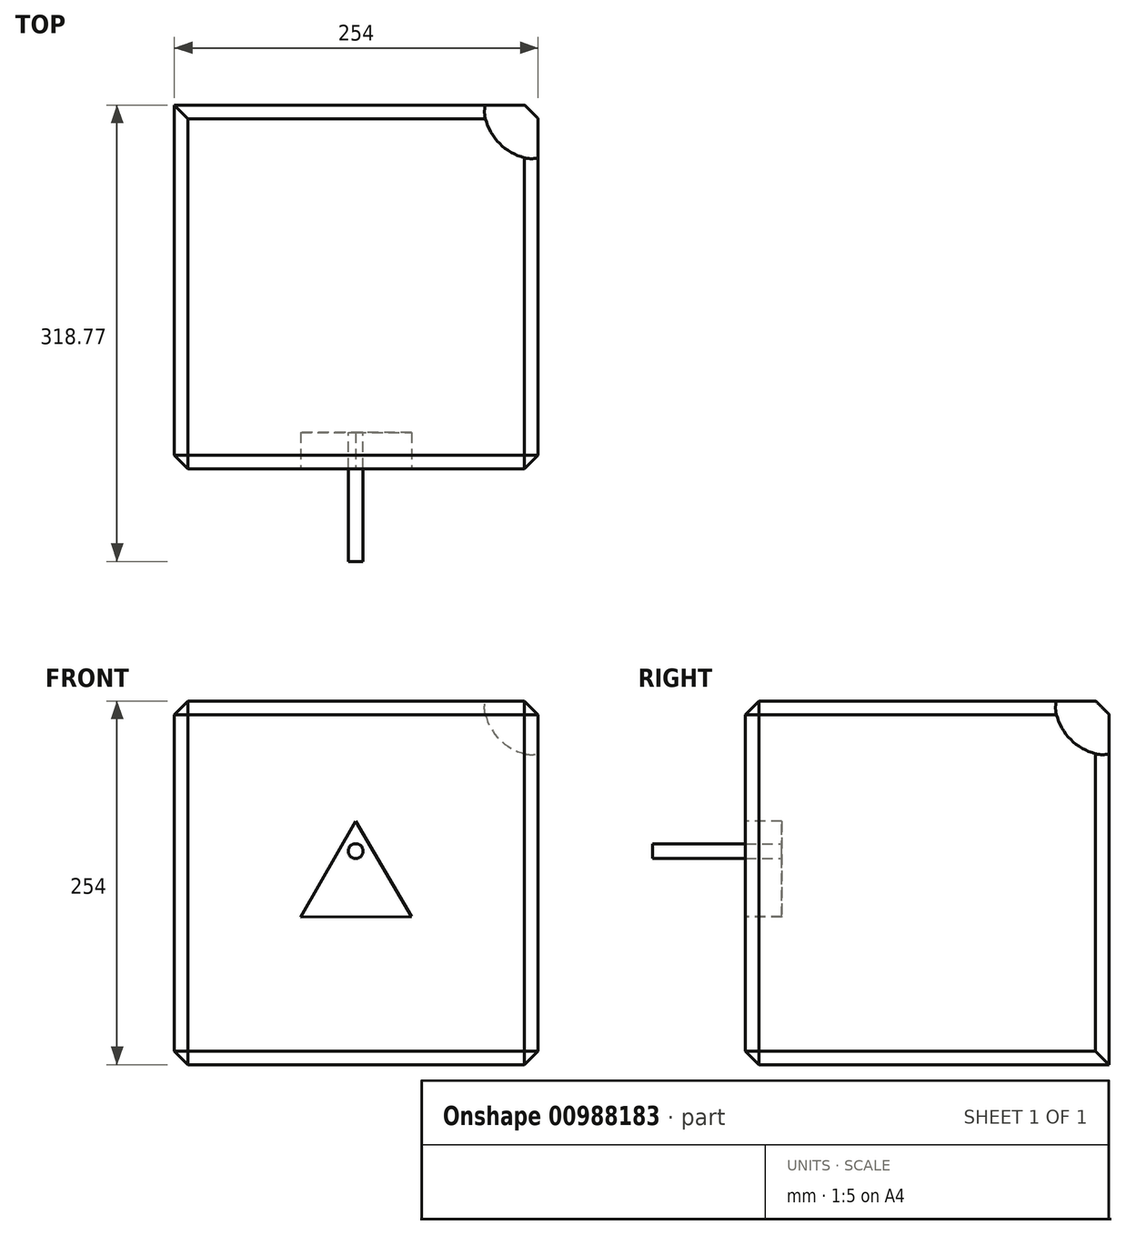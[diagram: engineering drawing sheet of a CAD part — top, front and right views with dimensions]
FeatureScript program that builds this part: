
annotation { "Feature Type Name" : "Feature", "Feature Type Description" : "" }
export const myFeature = defineFeature(function(context is Context, id is Id, definition is map)
    precondition{}
    {
        {
            var Q0;
            Q0=qCreatedBy(makeId("Top.planeOp"),FACE);
            var sketch = newSketch(context, id + "F0", { "sketchPlane" : qUnion([Q0])});
            skLineSegment(sketch, "E0.bottom", {"start": v(127, -127) * mm, "end": v(-127, -127) * mm});
            skLineSegment(sketch, "E0.top", {"start": v(127, 127) * mm, "end": v(-127, 127) * mm});
            skLineSegment(sketch, "E0.left", {"start": v(127, -127) * mm, "end": v(127, 127) * mm});
            skLineSegment(sketch, "E0.right", {"start": v(-127, -127) * mm, "end": v(-127, 127) * mm});
            skPoint(sketch, "E0.middle", {"position": v(0, 0) * mm});
            skSolve(sketch);
        }
        {
            var Q0;
            Q0=makeQuery(id+"F0.imprint","IMPRINT",FACE,{"disambiguationData":[TD([[makeQuery(id+"F0.imprint","IMPRINT",EDGE,{"derivedFrom":sQuery(id+"F0.wireOp",EDGE,"E0.bottom")}),-1.0]])]});
            extrude(context, id + "F1", {"entities" : qUnion([Q0]), "depth" : 254 * mm, "offsetDistance" : 25.4 * mm});
        }
        {
            var Q0;
            Q0=makeQuery(id+"F1.opExtrude","CAP_FACE",FACE,{"disambiguationData":[OSD([sQuery(id+"F0.wireOp",EDGE,"E0.bottom"),sQuery(id+"F0.wireOp",EDGE,"E0.top"),sQuery(id+"F0.wireOp",EDGE,"E0.left"),sQuery(id+"F0.wireOp",EDGE,"E0.right")])],"isStart":false});
            var sketch = newSketch(context, id + "F2", { "sketchPlane" : qUnion([Q0])});
            skCircle(sketch, "E1", {"center": v(127, 127) * mm, "radius": 38.1 * mm});
            skSolve(sketch);
        }
        {
            var Q0;
            {var subQ0=sQuery(id+"F2.wireOp",EDGE,"E1");var subQ1=makeQuery(id+"F1.opExtrude","CAP_EDGE",EDGE,{"disambiguationData":[OSD([sQuery(id+"F0.wireOp",EDGE,"E0.top")])],"isStart":false});var subQ2=makeQuery(id+"F2.imprint","INTERSECT",VERTEX,{"derivedFrom":[subQ1,subQ0]});Q0=makeQuery(id+"F2.imprint","IMPRINT",FACE,{"disambiguationData":[TD([[makeQuery(id+"F2.imprint","IMPRINT",EDGE,{"disambiguationData":[TD([[subQ2,-1.0]])],"derivedFrom":subQ0}),1.0]])]});}
            var Q1;
            Q1=sQuery(id+"F2.wireOp",EDGE,"E1");
            var Q2;
            Q2=makeQuery(id+"F1.opExtrude","CAP_EDGE",EDGE,{"disambiguationData":[OSD([sQuery(id+"F0.wireOp",EDGE,"E0.top")])],"isStart":false});
            var Q3;
            Q3=makeQuery(id+"F1.opExtrude","CAP_EDGE",EDGE,{"disambiguationData":[OSD([sQuery(id+"F0.wireOp",EDGE,"E0.top")])],"isStart":false});
            revolve(context, id + "F3", {"operationType" : NewBodyOperationType.REMOVE, "surfaceOperationType" : NewSurfaceOperationType.NEW, "entities" : qUnion([Q0]), "surfaceEntities" : qUnion([Q1, Q2]), "axis" : qUnion([Q3]), "revolveType" : RevolveType.FULL, "oppositeDirection" : true});
        }
        {
            var Q0;
            Q0=makeQuery(id+"F1.opExtrude","SWEPT_FACE",FACE,{"disambiguationData":[OSD([sQuery(id+"F0.wireOp",EDGE,"E0.bottom")])]});
            var sketch = newSketch(context, id + "F4", { "sketchPlane" : qUnion([Q0])});
            skCircle(sketch, "E2.cCircle", {"center": v(-0.29, 125.44) * mm, "radius": 44.57 * mm, "construction": true});
            skLineSegment(sketch, "E2.0", {"start": v(38.43, 103.36) * mm, "end": v(-38.76, 102.94) * mm});
            skLineSegment(sketch, "E2.1", {"start": v(-38.76, 102.94) * mm, "end": v(-0.53, 170) * mm});
            skLineSegment(sketch, "E2.2", {"start": v(-0.53, 170) * mm, "end": v(38.43, 103.36) * mm});
            skCircle(sketch, "E3", {"center": v(-0.29, 125.44) * mm, "radius": 7.28 * mm});
            skLineSegment(sketch, "E4", {"start": v(-0.53, 170) * mm, "end": v(-0.29, 87.45) * mm, "construction": true});
            skCircle(sketch, "E5", {"center": v(-0.47, 149.1) * mm, "radius": 5.23 * mm});
            skSolve(sketch);
        }
        {
            var Q0;
            Q0=makeQuery(id+"F4.imprint","IMPRINT",FACE,{"disambiguationData":[TD([[makeQuery(id+"F4.imprint","IMPRINT",EDGE,{"derivedFrom":sQuery(id+"F4.wireOp",EDGE,"E2.0")}),-1.0]])]});
            var Q1;
            Q1=makeQuery(id+"F4.imprint","IMPRINT",FACE,{"disambiguationData":[TD([[makeQuery(id+"F4.imprint","IMPRINT",EDGE,{"derivedFrom":sQuery(id+"F4.wireOp",EDGE,"E5")}),1.0]])]});
            var Q2;
            Q2=makeQuery(id+"F4.imprint","IMPRINT",FACE,{"disambiguationData":[TD([[makeQuery(id+"F4.imprint","IMPRINT",EDGE,{"derivedFrom":sQuery(id+"F4.wireOp",EDGE,"E3")}),1.0]])]});
            extrude(context, id + "F5", {"entities" : qUnion([Q0, Q1, Q2]), "operationType" : NewBodyOperationType.REMOVE, "oppositeDirection" : true, "depth" : 25.4 * mm, "offsetDistance" : 25.4 * mm});
        }
        {
            var Q0;
            Q0=makeQuery(id+"F4.imprint","IMPRINT",FACE,{"disambiguationData":[TD([[makeQuery(id+"F4.imprint","IMPRINT",EDGE,{"derivedFrom":sQuery(id+"F4.wireOp",EDGE,"E5")}),1.0]])]});
            extrude(context, id + "F6", {"entities" : qUnion([Q0]), "operationType" : NewBodyOperationType.ADD, "depth" : 129.54 * mm, "offsetDistance" : 25.4 * mm, "symmetric" : true});
        }
        {
            var Q0;
            Q0=makeQuery(id+"F1.opExtrude","CAP_EDGE",EDGE,{"disambiguationData":[OSD([sQuery(id+"F0.wireOp",EDGE,"E0.bottom")])],"isStart":false});
            var Q1;
            Q1=makeQuery(id+"F1.opExtrude","SWEPT_EDGE",EDGE,{"disambiguationData":[OSD([sQuery(id+"F0.wireOp",EDGE,"E0.bottom"),sQuery(id+"F0.wireOp",EDGE,"E0.left")])]});
            var Q2;
            Q2=makeQuery(id+"F1.opExtrude","CAP_EDGE",EDGE,{"disambiguationData":[OSD([sQuery(id+"F0.wireOp",EDGE,"E0.bottom")])],"isStart":true});
            var Q3;
            Q3=makeQuery(id+"F1.opExtrude","SWEPT_EDGE",EDGE,{"disambiguationData":[OSD([sQuery(id+"F0.wireOp",EDGE,"E0.bottom"),sQuery(id+"F0.wireOp",EDGE,"E0.right")])]});
            var Q4;
            Q4=makeQuery(id+"F1.opExtrude","CAP_EDGE",EDGE,{"disambiguationData":[OSD([sQuery(id+"F0.wireOp",EDGE,"E0.right")])],"isStart":false});
            var Q5;
            Q5=makeQuery(id+"F1.opExtrude","CAP_EDGE",EDGE,{"disambiguationData":[OSD([sQuery(id+"F0.wireOp",EDGE,"E0.right")])],"isStart":true});
            var Q6;
            Q6=makeQuery(id+"F1.opExtrude","CAP_EDGE",EDGE,{"disambiguationData":[OSD([sQuery(id+"F0.wireOp",EDGE,"E0.left")])],"isStart":true});
            var Q7;
            Q7=makeQuery(id+"F1.opExtrude","CAP_EDGE",EDGE,{"disambiguationData":[OSD([sQuery(id+"F0.wireOp",EDGE,"E0.left")])],"isStart":false});
            var Q8;
            Q8=makeQuery(id+"F1.opExtrude","CAP_EDGE",EDGE,{"disambiguationData":[OSD([sQuery(id+"F0.wireOp",EDGE,"E0.top")])],"isStart":false});
            var Q9;
            Q9=makeQuery(id+"F1.opExtrude","SWEPT_EDGE",EDGE,{"disambiguationData":[OSD([sQuery(id+"F0.wireOp",EDGE,"E0.top"),sQuery(id+"F0.wireOp",EDGE,"E0.left")])]});
            chamfer(context, id + "F7", {"entities" : qUnion([Q0, Q1, Q2, Q3, Q4, Q5, Q6, Q7, Q8, Q9]), "width" : 9.52 * mm, "tangentPropagation" : true});
        }
    });
